# Revit family: CH102.RFA
name_source: partatom
category: Generic Models
revit_build: Autodesk Revit MEP 2013 (Build: 20130531_2115(x64)
units: mm (PartAtom-declared; Revit-internal decimal feet)

## types (1)
- Zip ChillTap CH103 - Under-counter chiller
    Backflow Prevention Valve = Not Included
    Base Unit Finish = White Powder Coated Steel
    Cable Length and size (If Fitted) = 3 core 0.75mm2
    Capacity = 1.8 Litres
    Gross Weight (When Full) = 24.0kg
    Internal Filter (if fitted) = Yes - Submicron
    Location of Manufacturer = Australia
    Mains Pressure Limiting Valve = not included
    Mains Water Connection = 1/2" BSP - 15mm
    Mains Water Pressure _ Maximum = 0.7 MPa (7 bar)
    Mains Water Pressure _ Minimum = 0.17 MPa (1.7 bar)
    Manufacturer = Zip Industries(UK) Ltd
    Model = CH103
    Net Weight = 22.2kg
    Overall Height = 385mm
    Overall Length = 290mm
    Overall Width = 355mm
    Power Rating = 300W
    Power Supply (Voltage) = 240V (50~60Hz)
    Product Range = Chilltap
    Refridgerant = Non-toxic R134A.
    Shape = Rectangular
    Supply Phase = 1 Phase
    Tank Construction Material = Stainless steel
    Type = Fan cooled condenser with compressor.
    Type Comments = Under-counter chiller
    URL = www.zipindustries.co.uk
    Unit Access Clearance Bottom = Floor Standing
    Unit Access Clearance Left = 50mm
    Unit Access Clearance Rear = 20mm
    Unit Access Clearance Top = 200mm
    Unit Access Clearance right = 50mm
    Volume Dispensed per hour = Rated at 140 glasses per hour at <10 ºC.
    WRAS Approved = Yes
    Warranty ID = 12 MONTHS

## geometry (parser evidence)
native form markers: Sweep x2
no freeform markers — native parametric forms only
